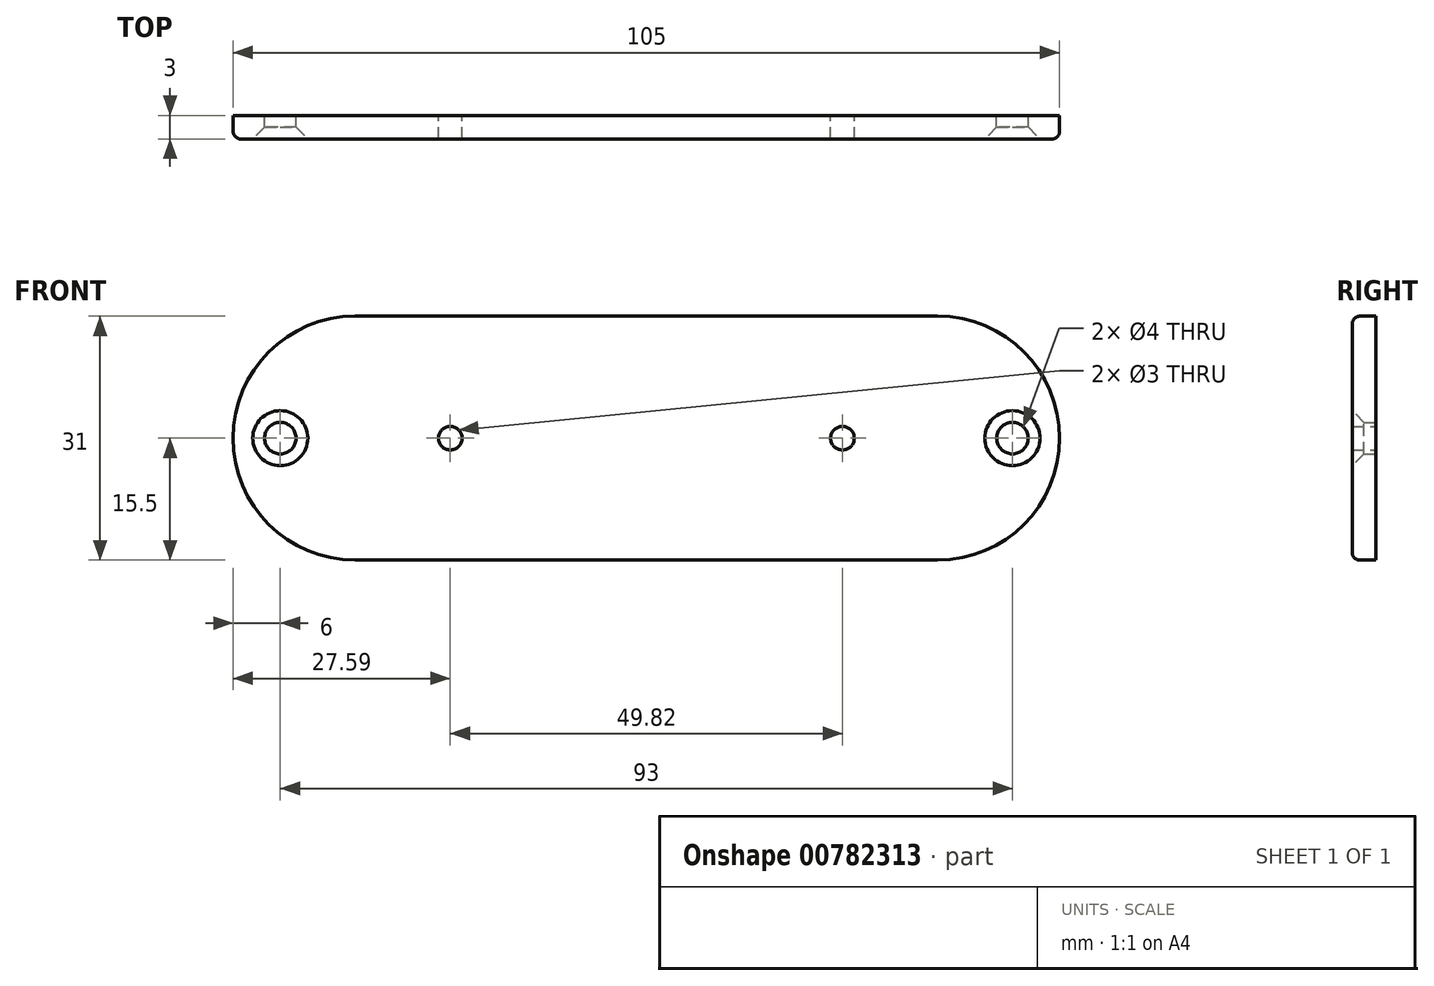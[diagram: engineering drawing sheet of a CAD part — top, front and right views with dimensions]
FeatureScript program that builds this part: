
annotation { "Feature Type Name" : "Feature", "Feature Type Description" : "" }
export const myFeature = defineFeature(function(context is Context, id is Id, definition is map)
    precondition{}
    {
        {
            var Q0;
            Q0=qCreatedBy(makeId("Front.planeOp"),FACE);
            var sketch = newSketch(context, id + "F0", { "sketchPlane" : qUnion([Q0])});
            skLineSegment(sketch, "E0.bottom", {"start": v(-37, 15.5) * mm, "end": v(37, 15.5) * mm});
            skLineSegment(sketch, "E0.top", {"start": v(-37, -15.5) * mm, "end": v(37, -15.5) * mm});
            skPoint(sketch, "E0.middle", {"position": v(0, 0) * mm});
            skArc(sketch, "E1", {"start": v(37, -15.5) * mm, "mid": v(52.5, 0) * mm, "end": v(37, 15.5) * mm});
            skPoint(sketch, "E1.centerSnap0", {"position": v(52.5, 0) * mm});
            skPoint(sketch, "E2.orphan", {"position": v(52.5, 15.5) * mm});
            skPoint(sketch, "E3.orphan", {"position": v(52.5, -15.5) * mm});
            skArc(sketch, "E4.MirrorCS", {"start": v(-37, -15.5) * mm, "mid": v(-52.5, 0) * mm, "end": v(-37, 15.5) * mm});
            skPoint(sketch, "E5.orphan", {"position": v(-52.5, 15.5) * mm});
            skPoint(sketch, "E6.orphan", {"position": v(-52.5, -15.5) * mm});
            skCircle(sketch, "E7", {"center": v(-46.5, 0) * mm, "radius": 2 * mm});
            skCircle(sketch, "E8", {"center": v(-24.9, 0) * mm, "radius": 1.5 * mm});
            skCircle(sketch, "E9.MirrorC", {"center": v(24.9, 0) * mm, "radius": 1.5 * mm});
            skCircle(sketch, "E10.MirrorC", {"center": v(46.5, 0) * mm, "radius": 2 * mm});
            skSolve(sketch);
        }
        {
            var Q0;
            Q0 = qSketchRegion(id + "F0", true);
            extrude(context, id + "F1", {"entities" : qUnion([Q0]), "depth" : 3 * mm, "offsetDistance" : 25 * mm});
        }
        {
            var Q0;
            Q0=makeQuery(id+"F1.opExtrude","CAP_EDGE",EDGE,{"disambiguationData":[OSD([sQuery(id+"F0.wireOp",EDGE,"E0.bottom")])],"isStart":false});
            fillet(context, id + "F2", {"entities" : qUnion([Q0]), "radius" : 1 * mm, "tangentPropagation" : true, "allowEdgeOverflow" : false});
        }
        {
            var Q0;
            Q0=makeQuery(id+"F1.opExtrude","CAP_EDGE",EDGE,{"disambiguationData":[OSD([sQuery(id+"F0.wireOp",EDGE,"E7")])],"isStart":false});
            var Q1;
            Q1=makeQuery(id+"F1.opExtrude","CAP_EDGE",EDGE,{"disambiguationData":[OSD([sQuery(id+"F0.wireOp",EDGE,"E10.MirrorC")])],"isStart":false});
            chamfer(context, id + "F3", {"entities" : qUnion([Q0, Q1]), "width" : 1.5 * mm, "tangentPropagation" : true});
        }
    });
